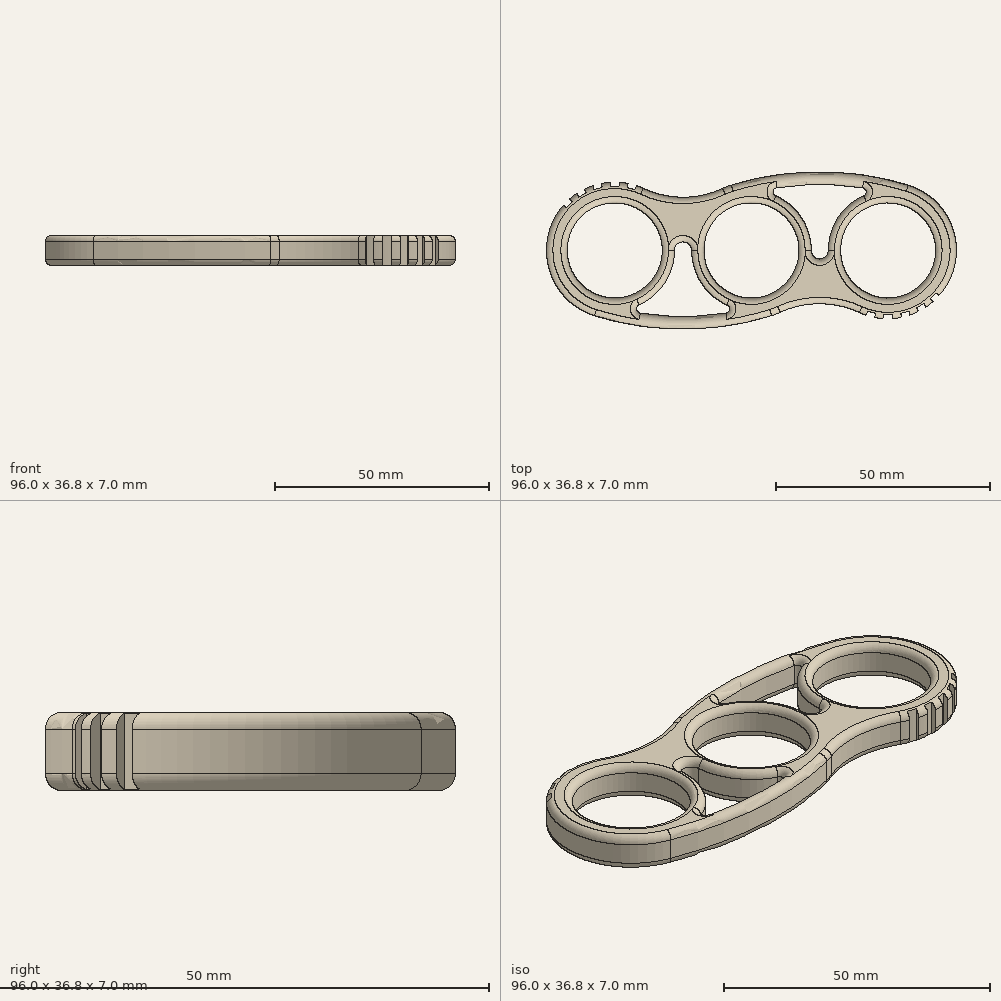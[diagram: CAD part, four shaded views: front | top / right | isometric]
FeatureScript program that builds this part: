
annotation { "Feature Type Name" : "Feature", "Feature Type Description" : "" }
export const myFeature = defineFeature(function(context is Context, id is Id, definition is map)
    precondition{}
    {
        {
            var Q0;
            Q0=qCreatedBy(makeId("Top.planeOp"),FACE);
            var sketch = newSketch(context, id + "F0", { "sketchPlane" : qUnion([Q0])});
            skArc(sketch, "E0", {"start": v(4.74, -15.28) * mm, "mid": v(5.75, -14.93) * mm, "end": v(6.74, -14.51) * mm});
            skArc(sketch, "E1", {"start": v(-25.26, 14.51) * mm, "mid": v(-45.87, 7.97) * mm, "end": v(-41.14, -13.13) * mm});
            skArc(sketch, "E2", {"start": v(25.26, -14.51) * mm, "mid": v(45.87, -7.97) * mm, "end": v(41.14, 13.13) * mm});
            skArc(sketch, "E3", {"start": v(-25.26, 14.51) * mm, "mid": v(-16, 12.47) * mm, "end": v(-6.74, 14.51) * mm});
            skArc(sketch, "E4", {"start": v(25.26, -14.51) * mm, "mid": v(16, -12.47) * mm, "end": v(6.74, -14.51) * mm});
            skArc(sketch, "E5.trimOffspring", {"start": v(-4.74, 15.28) * mm, "mid": v(-5.75, 14.93) * mm, "end": v(-6.74, 14.51) * mm});
            skArc(sketch, "E6.trimOffspring", {"start": v(-41.14, -13.13) * mm, "mid": v(-39.02, -14.38) * mm, "end": v(-36.74, -15.28) * mm});
            skArc(sketch, "E7.trimOffspring", {"start": v(41.14, 13.13) * mm, "mid": v(39.02, 14.38) * mm, "end": v(36.74, 15.28) * mm});
            skArc(sketch, "E8", {"start": v(36.74, 15.28) * mm, "mid": v(16, 18.42) * mm, "end": v(-4.74, 15.28) * mm});
            skArc(sketch, "E9", {"start": v(-36.74, -15.28) * mm, "mid": v(-16, -18.42) * mm, "end": v(4.74, -15.28) * mm});
            skSolve(sketch);
        }
        {
            var Q0;
            Q0=qSketchRegion(id+"F0",true);
            extrude(context, id + "F1", {"entities" : qUnion([Q0]), "depth" : 7 * mm});
        }
        {
            var Q0;
            Q0=makeQuery(id+"F1.opExtrude","CAP_FACE",FACE,{"disambiguationData":[OSD([sQuery(id+"F0.wireOp",EDGE,"E0"),sQuery(id+"F0.wireOp",EDGE,"E1"),sQuery(id+"F0.wireOp",EDGE,"E2"),sQuery(id+"F0.wireOp",EDGE,"E3"),sQuery(id+"F0.wireOp",EDGE,"U9qsNBJu-XeLE-ORlb-NQLH-GNNNRFqsx3aL"),sQuery(id+"F0.wireOp",EDGE,"KtAAOo4r-4s1N-9Oyr-xdw8-T3c3s2v9GRLw"),sQuery(id+"F0.wireOp",EDGE,"E4"),sQuery(id+"F0.wireOp",EDGE,"E5.trimOffspring")])],"isStart":false});
            var sketch = newSketch(context, id + "F2", { "sketchPlane" : qUnion([Q0])});
            skCircle(sketch, "E10", {"center": v(0, 0) * mm, "radius": 11.12 * mm});
            skPoint(sketch, "E10.perimeterSnap0", {"position": v(-5.75, 14.93) * mm});
            skPoint(sketch, "E10.perimeterSnap1", {"position": v(-16, 12.47) * mm});
            skCircle(sketch, "E11", {"center": v(-32, 0) * mm, "radius": 11.12 * mm});
            skCircle(sketch, "E12", {"center": v(32, 0) * mm, "radius": 11.12 * mm});
            skSolve(sketch);
        }
        {
            var Q0;
            Q0=qSketchRegion(id+"F2",true);
            extrude(context, id + "F3", {"entities" : qUnion([Q0]), "operationType" : NewBodyOperationType.REMOVE, "endBound" : BoundingType.THROUGH_ALL, "oppositeDirection" : true, "depth" : 25 * mm});
        }
        {
            var Q0;
            Q0=makeQuery(id+"F1.opExtrude","CAP_FACE",FACE,{"disambiguationData":[OSD([sQuery(id+"F0.wireOp",EDGE,"E0"),sQuery(id+"F0.wireOp",EDGE,"E1"),sQuery(id+"F0.wireOp",EDGE,"E2"),sQuery(id+"F0.wireOp",EDGE,"E3"),sQuery(id+"F0.wireOp",EDGE,"E4"),sQuery(id+"F0.wireOp",EDGE,"E5.trimOffspring"),sQuery(id+"F0.wireOp",EDGE,"hpOvTq7A-kyfb-DXtC-TEhA-or5gheuMUULX"),sQuery(id+"F0.wireOp",EDGE,"wBePiWC6-iGpO-Zq4v-ABb4-8q9CdOJLcKBH"),sQuery(id+"F0.wireOp",EDGE,"ZJYLghvL-pm70-bnTZ-rQ5k-KHeNHSjt74Mt"),sQuery(id+"F0.wireOp",EDGE,"E6.trimOffspring"),sQuery(id+"F0.wireOp",EDGE,"bhJmbQDj-123R-5zu5-01mg-wOOI3Yt0Lu7z"),sQuery(id+"F0.wireOp",EDGE,"YeVEtyaY-yGgt-7S4g-LW9z-fGMiD1Vh3O3b"),sQuery(id+"F0.wireOp",EDGE,"oH4s39by-uDe5-ougK-N1i2-lCchJTmDNlGg"),sQuery(id+"F0.wireOp",EDGE,"E7.trimOffspring"),sQuery(id+"F0.wireOp",EDGE,"E8"),sQuery(id+"F0.wireOp",EDGE,"E9")])],"isStart":false});
            var sketch = newSketch(context, id + "F4", { "sketchPlane" : qUnion([Q0])});
            skArc(sketch, "E13", {"start": v(-26, -14.67) * mm, "mid": v(-16, -15.42) * mm, "end": v(-6, -14.67) * mm});
            skArc(sketch, "E14", {"start": v(-14, 0) * mm, "mid": v(-11.75, -7.6) * mm, "end": v(-5.73, -12.77) * mm});
            skArc(sketch, "E15", {"start": v(14, 0) * mm, "mid": v(16, -2) * mm, "end": v(18, 0) * mm});
            skArc(sketch, "E16", {"start": v(-14, 0) * mm, "mid": v(-16, 2) * mm, "end": v(-18, 0) * mm});
            skArc(sketch, "E17.trimOffspring", {"start": v(-26.27, -12.77) * mm, "mid": v(-20.25, -7.6) * mm, "end": v(-18, 0) * mm});
            skArc(sketch, "E18.trimOffspring", {"start": v(14, 0) * mm, "mid": v(11.75, 7.6) * mm, "end": v(5.73, 12.77) * mm});
            skArc(sketch, "E19.trimOffspring", {"start": v(26.27, 12.77) * mm, "mid": v(20.25, 7.6) * mm, "end": v(18, 0) * mm});
            skArc(sketch, "E20.trimOffspring", {"start": v(26, 14.67) * mm, "mid": v(16, 15.42) * mm, "end": v(6, 14.67) * mm});
            skPoint(sketch, "E21.visualSharp", {"position": v(-30.25, -13.9) * mm});
            skArc(sketch, "E21.filletArc", {"start": v(-26.27, -12.77) * mm, "mid": v(-26.85, -13.82) * mm, "end": v(-26, -14.67) * mm});
            skPoint(sketch, "E22.visualSharp", {"position": v(-1.75, -13.9) * mm});
            skArc(sketch, "E22.filletArc", {"start": v(-6, -14.67) * mm, "mid": v(-5.15, -13.82) * mm, "end": v(-5.73, -12.77) * mm});
            skPoint(sketch, "E23.visualSharp", {"position": v(1.75, 13.9) * mm});
            skArc(sketch, "E23.filletArc", {"start": v(6, 14.67) * mm, "mid": v(5.15, 13.82) * mm, "end": v(5.73, 12.77) * mm});
            skPoint(sketch, "E24.visualSharp", {"position": v(30.25, 13.9) * mm});
            skArc(sketch, "E24.filletArc", {"start": v(26.27, 12.77) * mm, "mid": v(26.85, 13.82) * mm, "end": v(26, 14.67) * mm});
            skSolve(sketch);
        }
        {
            var Q0;
            Q0 = qSketchRegion(id + "F4", true);
            extrude(context, id + "F5", {"entities" : qUnion([Q0]), "operationType" : NewBodyOperationType.REMOVE, "endBound" : BoundingType.THROUGH_ALL, "oppositeDirection" : true, "depth" : 25 * mm});
        }
        {
            var Q0;
            Q0=makeQuery(id+"F1.opExtrude","CAP_FACE",FACE,{"disambiguationData":[OSD([sQuery(id+"F0.wireOp",EDGE,"E0"),sQuery(id+"F0.wireOp",EDGE,"E1"),sQuery(id+"F0.wireOp",EDGE,"E2"),sQuery(id+"F0.wireOp",EDGE,"E3"),sQuery(id+"F0.wireOp",EDGE,"E4"),sQuery(id+"F0.wireOp",EDGE,"E5.trimOffspring"),sQuery(id+"F0.wireOp",EDGE,"hpOvTq7A-kyfb-DXtC-TEhA-or5gheuMUULX"),sQuery(id+"F0.wireOp",EDGE,"wBePiWC6-iGpO-Zq4v-ABb4-8q9CdOJLcKBH"),sQuery(id+"F0.wireOp",EDGE,"ZJYLghvL-pm70-bnTZ-rQ5k-KHeNHSjt74Mt"),sQuery(id+"F0.wireOp",EDGE,"E6.trimOffspring"),sQuery(id+"F0.wireOp",EDGE,"bhJmbQDj-123R-5zu5-01mg-wOOI3Yt0Lu7z"),sQuery(id+"F0.wireOp",EDGE,"YeVEtyaY-yGgt-7S4g-LW9z-fGMiD1Vh3O3b"),sQuery(id+"F0.wireOp",EDGE,"oH4s39by-uDe5-ougK-N1i2-lCchJTmDNlGg"),sQuery(id+"F0.wireOp",EDGE,"E7.trimOffspring"),sQuery(id+"F0.wireOp",EDGE,"E8"),sQuery(id+"F0.wireOp",EDGE,"E9")])],"isStart":false});
            var Q1;
            Q1=makeQuery(id+"F1.opExtrude","CAP_FACE",FACE,{"disambiguationData":[OSD([sQuery(id+"F0.wireOp",EDGE,"E0"),sQuery(id+"F0.wireOp",EDGE,"E1"),sQuery(id+"F0.wireOp",EDGE,"E2"),sQuery(id+"F0.wireOp",EDGE,"E3"),sQuery(id+"F0.wireOp",EDGE,"E4"),sQuery(id+"F0.wireOp",EDGE,"E5.trimOffspring"),sQuery(id+"F0.wireOp",EDGE,"hpOvTq7A-kyfb-DXtC-TEhA-or5gheuMUULX"),sQuery(id+"F0.wireOp",EDGE,"wBePiWC6-iGpO-Zq4v-ABb4-8q9CdOJLcKBH"),sQuery(id+"F0.wireOp",EDGE,"ZJYLghvL-pm70-bnTZ-rQ5k-KHeNHSjt74Mt"),sQuery(id+"F0.wireOp",EDGE,"E6.trimOffspring"),sQuery(id+"F0.wireOp",EDGE,"bhJmbQDj-123R-5zu5-01mg-wOOI3Yt0Lu7z"),sQuery(id+"F0.wireOp",EDGE,"YeVEtyaY-yGgt-7S4g-LW9z-fGMiD1Vh3O3b"),sQuery(id+"F0.wireOp",EDGE,"oH4s39by-uDe5-ougK-N1i2-lCchJTmDNlGg"),sQuery(id+"F0.wireOp",EDGE,"E7.trimOffspring"),sQuery(id+"F0.wireOp",EDGE,"E8"),sQuery(id+"F0.wireOp",EDGE,"E9")])],"isStart":true});
            fillet(context, id + "F6", {"entities" : qUnion([Q0, Q1]), "radius" : 1.5 * mm, "tangentPropagation" : true, "allowEdgeOverflow" : false});
        }
        {
            var Q0;
            Q0=makeQuery(id+"F1.opExtrude","CAP_FACE",FACE,{"disambiguationData":[OSD([sQuery(id+"F0.wireOp",EDGE,"E0"),sQuery(id+"F0.wireOp",EDGE,"E1"),sQuery(id+"F0.wireOp",EDGE,"E2"),sQuery(id+"F0.wireOp",EDGE,"E3"),sQuery(id+"F0.wireOp",EDGE,"E4"),sQuery(id+"F0.wireOp",EDGE,"E5.trimOffspring"),sQuery(id+"F0.wireOp",EDGE,"E6.trimOffspring"),sQuery(id+"F0.wireOp",EDGE,"E7.trimOffspring"),sQuery(id+"F0.wireOp",EDGE,"E8"),sQuery(id+"F0.wireOp",EDGE,"E9")])],"isStart":false});
            var sketch = newSketch(context, id + "F7", { "sketchPlane" : qUnion([Q0])});
            skArc(sketch, "E25", {"start": v(-31, 14.97) * mm, "mid": v(-32, 15) * mm, "end": v(-33, 14.97) * mm});
            skArc(sketch, "E26", {"start": v(-31, 16.97) * mm, "mid": v(-32, 17) * mm, "end": v(-33, 16.97) * mm});
            skLineSegment(sketch, "E27.0", {"start": v(-31, 14.97) * mm, "end": v(-31, 16.97) * mm});
            skLineSegment(sketch, "E28.0", {"start": v(-33, 14.97) * mm, "end": v(-33, 16.97) * mm});
            skArc(sketch, "E29.1.0", {"start": v(-34.9, 14.72) * mm, "mid": v(-35.88, 14.49) * mm, "end": v(-36.84, 14.2) * mm});
            skLineSegment(sketch, "E29.1.1", {"start": v(-34.9, 14.72) * mm, "end": v(-35.43, 16.65) * mm});
            skLineSegment(sketch, "E29.1.2", {"start": v(-36.84, 14.2) * mm, "end": v(-37.36, 16.13) * mm});
            skArc(sketch, "E29.1.3", {"start": v(-35.43, 16.65) * mm, "mid": v(-36.4, 16.42) * mm, "end": v(-37.36, 16.13) * mm});
            skArc(sketch, "E29.2.0", {"start": v(-38.62, 13.46) * mm, "mid": v(-39.5, 13) * mm, "end": v(-40.35, 12.46) * mm});
            skLineSegment(sketch, "E29.2.1", {"start": v(-38.62, 13.46) * mm, "end": v(-39.62, 15.2) * mm});
            skLineSegment(sketch, "E29.2.2", {"start": v(-40.35, 12.46) * mm, "end": v(-41.35, 14.2) * mm});
            skArc(sketch, "E29.2.3", {"start": v(-39.62, 15.2) * mm, "mid": v(-40.5, 14.72) * mm, "end": v(-41.35, 14.2) * mm});
            skArc(sketch, "E29.3.0", {"start": v(-41.88, 11.3) * mm, "mid": v(-42.6, 10.6) * mm, "end": v(-43.3, 9.88) * mm});
            skLineSegment(sketch, "E29.3.1", {"start": v(-41.88, 11.3) * mm, "end": v(-43.3, 12.7) * mm});
            skLineSegment(sketch, "E29.3.2", {"start": v(-43.3, 9.88) * mm, "end": v(-44.7, 11.3) * mm});
            skArc(sketch, "E29.3.3", {"start": v(-43.3, 12.7) * mm, "mid": v(-44.02, 12.02) * mm, "end": v(-44.7, 11.3) * mm});
            skArc(sketch, "E30.1.1", {"start": v(-27.16, 14.2) * mm, "mid": v(-28.12, 14.49) * mm, "end": v(-29.1, 14.72) * mm});
            skLineSegment(sketch, "E30.1.2", {"start": v(-29.1, 14.72) * mm, "end": v(-28.57, 16.65) * mm});
            skLineSegment(sketch, "E30.1.3", {"start": v(-27.16, 14.2) * mm, "end": v(-26.64, 16.13) * mm});
            skArc(sketch, "E30.1.4", {"start": v(-26.64, 16.13) * mm, "mid": v(-27.6, 16.42) * mm, "end": v(-28.57, 16.65) * mm});
            skLineSegment(sketch, "E31.MirrorCS", {"start": v(31, -14.97) * mm, "end": v(31, -16.97) * mm});
            skArc(sketch, "E32.MirrorCS", {"start": v(38.62, -13.46) * mm, "mid": v(39.5, -13) * mm, "end": v(40.35, -12.46) * mm});
            skLineSegment(sketch, "E33.MirrorCS", {"start": v(41.88, -11.3) * mm, "end": v(43.3, -12.7) * mm});
            skArc(sketch, "E34.MirrorCS", {"start": v(34.9, -14.72) * mm, "mid": v(35.88, -14.49) * mm, "end": v(36.84, -14.2) * mm});
            skLineSegment(sketch, "E35.MirrorCS", {"start": v(29.1, -14.72) * mm, "end": v(28.57, -16.65) * mm});
            skLineSegment(sketch, "E36.MirrorCS", {"start": v(27.16, -14.2) * mm, "end": v(26.64, -16.13) * mm});
            skArc(sketch, "E37.MirrorCS", {"start": v(41.88, -11.3) * mm, "mid": v(42.6, -10.6) * mm, "end": v(43.3, -9.88) * mm});
            skArc(sketch, "E38.MirrorCS", {"start": v(31, -14.97) * mm, "mid": v(32, -15) * mm, "end": v(33, -14.97) * mm});
            skArc(sketch, "E39.MirrorCS", {"start": v(26.64, -16.13) * mm, "mid": v(27.6, -16.42) * mm, "end": v(28.57, -16.65) * mm});
            skArc(sketch, "E40.MirrorCS", {"start": v(27.16, -14.2) * mm, "mid": v(28.12, -14.49) * mm, "end": v(29.1, -14.72) * mm});
            skLineSegment(sketch, "E41.MirrorCS", {"start": v(33, -14.97) * mm, "end": v(33, -16.97) * mm});
            skLineSegment(sketch, "E42.MirrorCS", {"start": v(34.9, -14.72) * mm, "end": v(35.43, -16.65) * mm});
            skLineSegment(sketch, "E43.MirrorCS", {"start": v(43.3, -9.88) * mm, "end": v(44.7, -11.3) * mm});
            skArc(sketch, "E44.MirrorCS", {"start": v(39.62, -15.2) * mm, "mid": v(40.5, -14.72) * mm, "end": v(41.35, -14.2) * mm});
            skArc(sketch, "E45.MirrorCS", {"start": v(35.43, -16.65) * mm, "mid": v(36.4, -16.42) * mm, "end": v(37.36, -16.13) * mm});
            skLineSegment(sketch, "E46.MirrorCS", {"start": v(40.35, -12.46) * mm, "end": v(41.35, -14.2) * mm});
            skArc(sketch, "E47.MirrorCS", {"start": v(43.3, -12.7) * mm, "mid": v(44.02, -12.02) * mm, "end": v(44.7, -11.3) * mm});
            skLineSegment(sketch, "E48.MirrorCS", {"start": v(36.84, -14.2) * mm, "end": v(37.36, -16.13) * mm});
            skLineSegment(sketch, "E49.MirrorCS", {"start": v(38.62, -13.46) * mm, "end": v(39.62, -15.2) * mm});
            skArc(sketch, "E50.MirrorCS", {"start": v(31, -16.97) * mm, "mid": v(32, -17) * mm, "end": v(33, -16.97) * mm});
            skSolve(sketch);
        }
        {
            var Q0;
            Q0 = qSketchRegion(id + "F7", true);
            extrude(context, id + "F8", {"entities" : qUnion([Q0]), "operationType" : NewBodyOperationType.REMOVE, "endBound" : BoundingType.THROUGH_ALL, "oppositeDirection" : true, "depth" : 25 * mm});
        }
    });
